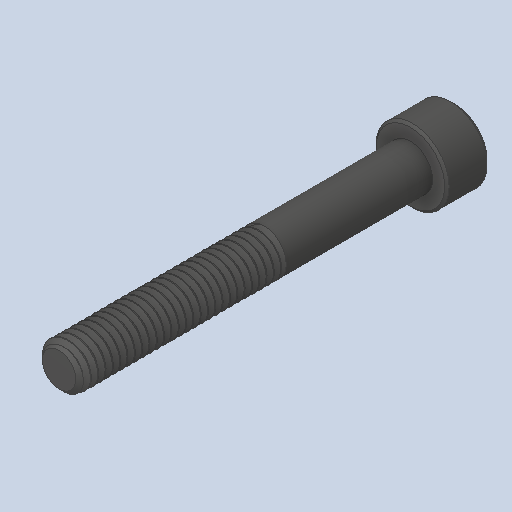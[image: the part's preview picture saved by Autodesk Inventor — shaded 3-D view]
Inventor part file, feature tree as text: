
AUTODESK INVENTOR PART (.ipt)
format: ipt  version: 2023 (Build 270158000, 158)  size: 688,128 bytes
history: native  units: in
note: dims shown in document units (in); Inventor stores cm internally (conversion verified against a paired STEP export)
features: chamfer x1
ambient origin geometry x8: Origin, YZ Plane, XZ Plane, XY Plane, X Axis, Y Axis, Z Axis, Center Point
bodies: Solid1 (feature_tree)
feature tree (1):
  chamfer  "Chamfer2"  [1 undecoded]
note: 1 required parameter value undecoded (feature->parameter linkage not recoverable at this tier; creation-order binding heuristic only, values carry confidence <= 0.55)
